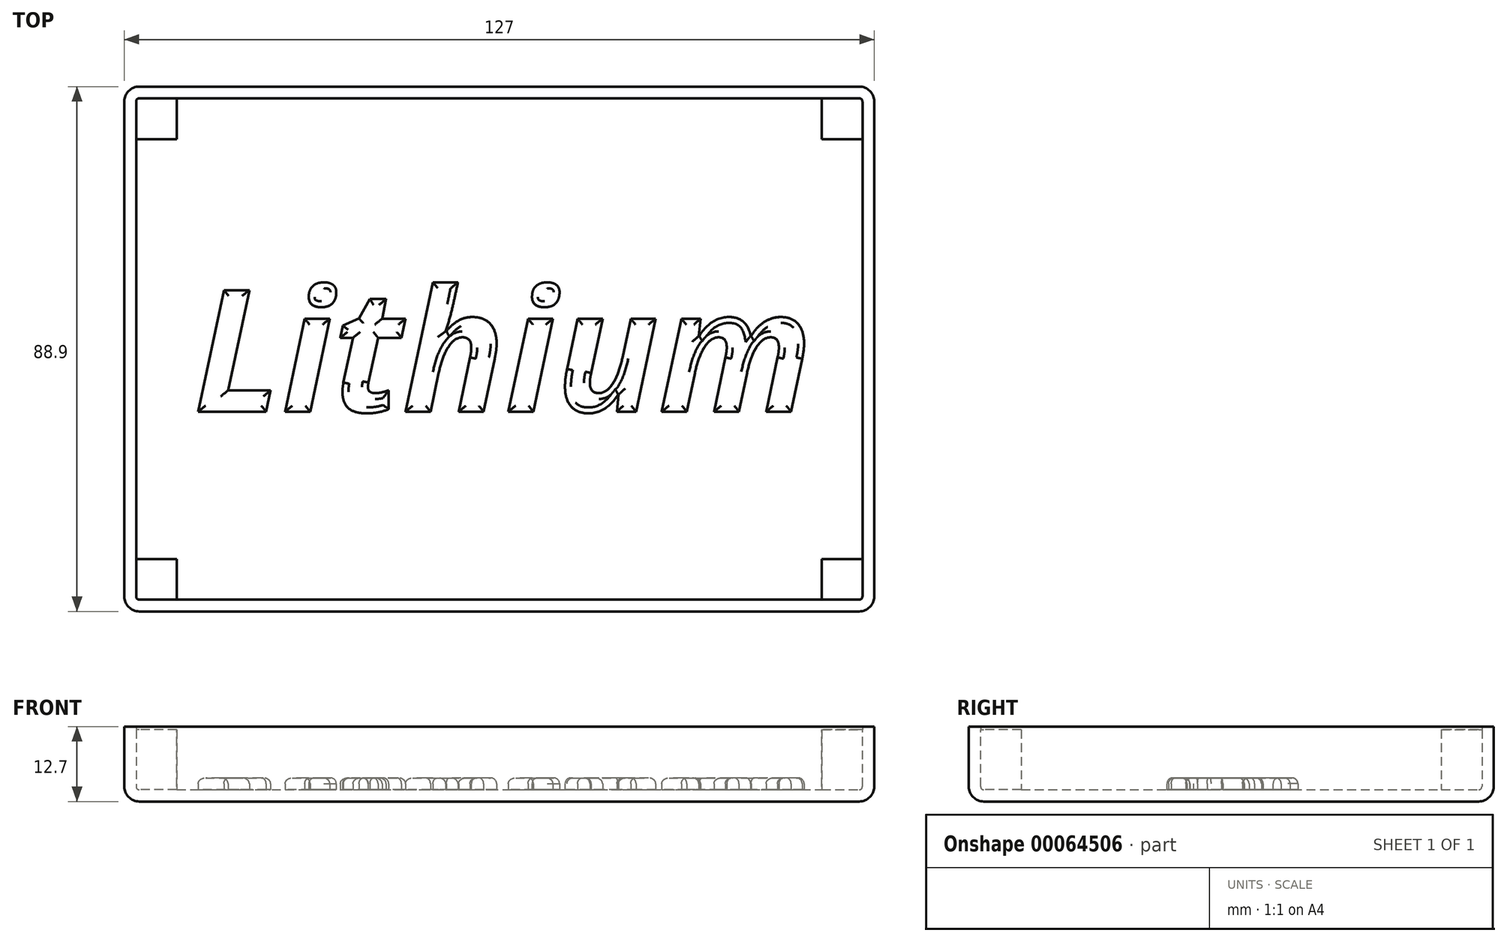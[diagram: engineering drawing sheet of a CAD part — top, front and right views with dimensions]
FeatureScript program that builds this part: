
annotation { "Feature Type Name" : "Feature", "Feature Type Description" : "" }
export const myFeature = defineFeature(function(context is Context, id is Id, definition is map)
    precondition{}
    {
        {
            var Q0;
            Q0=qCreatedBy(makeId("Top.planeOp"),FACE);
            var sketch = newSketch(context, id + "F0", { "sketchPlane" : qUnion([Q0])});
            skLineSegment(sketch, "E0.rect.bottom", {"start": v(63.5, 44.45) * mm, "end": v(-63.5, 44.45) * mm});
            skLineSegment(sketch, "E0.rect.top", {"start": v(63.5, -44.45) * mm, "end": v(-63.5, -44.45) * mm});
            skLineSegment(sketch, "E0.rect.left", {"start": v(63.5, 44.45) * mm, "end": v(63.5, -44.45) * mm});
            skLineSegment(sketch, "E0.rect.right", {"start": v(-63.5, 44.45) * mm, "end": v(-63.5, -44.45) * mm});
            skPoint(sketch, "E0.rect.middle", {"position": v(0, 0) * mm});
            skSolve(sketch);
        }
        {
            var Q0;
            Q0 = qSketchRegion(id + "F0", true);
            extrude(context, id + "F1", {"entities" : qUnion([Q0]), "depth" : 12.7 * mm});
        }
        {
            var Q0;
            Q0=makeQuery(id+"F1.opExtrude","SWEPT_EDGE",EDGE,{"disambiguationData":[OSD([sQuery(id+"F0.wireOp",EDGE,"E0.rect.top"),sQuery(id+"F0.wireOp",EDGE,"E0.rect.right")])]});
            var Q1;
            Q1=makeQuery(id+"F1.opExtrude","SWEPT_EDGE",EDGE,{"disambiguationData":[OSD([sQuery(id+"F0.wireOp",EDGE,"E0.rect.bottom"),sQuery(id+"F0.wireOp",EDGE,"E0.rect.right")])]});
            var Q2;
            Q2=makeQuery(id+"F1.opExtrude","SWEPT_EDGE",EDGE,{"disambiguationData":[OSD([sQuery(id+"F0.wireOp",EDGE,"E0.rect.bottom"),sQuery(id+"F0.wireOp",EDGE,"E0.rect.left")])]});
            var Q3;
            Q3=makeQuery(id+"F1.opExtrude","SWEPT_EDGE",EDGE,{"disambiguationData":[OSD([sQuery(id+"F0.wireOp",EDGE,"E0.rect.top"),sQuery(id+"F0.wireOp",EDGE,"E0.rect.left")])]});
            var Q4;
            Q4=makeQuery(id+"F1.opExtrude","CAP_FACE",FACE,{"disambiguationData":[OSD([sQuery(id+"F0.wireOp",EDGE,"E0.rect.bottom"),sQuery(id+"F0.wireOp",EDGE,"E0.rect.top"),sQuery(id+"F0.wireOp",EDGE,"E0.rect.left"),sQuery(id+"F0.wireOp",EDGE,"E0.rect.right")])],"isStart":true});
            fillet(context, id + "F2", {"entities" : qUnion([Q0, Q1, Q2, Q3, Q4]), "radius" : 2.54 * mm, "tangentPropagation" : true, "allowEdgeOverflow" : false});
        }
        {
            var Q0;
            Q0=makeQuery(id+"F1.opExtrude","CAP_FACE",FACE,{"disambiguationData":[OSD([sQuery(id+"F0.wireOp",EDGE,"E0.rect.bottom"),sQuery(id+"F0.wireOp",EDGE,"E0.rect.top"),sQuery(id+"F0.wireOp",EDGE,"E0.rect.left"),sQuery(id+"F0.wireOp",EDGE,"E0.rect.right")])],"isStart":false});
            shell(context, id + "F3", {"entities" : qUnion([Q0]), "thickness" : 2 * mm});
        }
        {
            var Q0;
            Q0=makeQuery(id+"F3.opShell","OFFSET_FACE",FACE,{"disambiguationData":[OSD([sQuery(id+"F0.wireOp",EDGE,"E0.rect.bottom"),sQuery(id+"F0.wireOp",EDGE,"E0.rect.top"),sQuery(id+"F0.wireOp",EDGE,"E0.rect.left"),sQuery(id+"F0.wireOp",EDGE,"E0.rect.right")])]});
            var sketch = newSketch(context, id + "F4", { "sketchPlane" : qUnion([Q0])});
            skLineSegment(sketch, "E1.bottom", {"start": v(-60.96, 41.91) * mm, "end": v(-54.61, 41.91) * mm});
            skLineSegment(sketch, "E1.top", {"start": v(-60.96, 35.56) * mm, "end": v(-54.61, 35.56) * mm});
            skLineSegment(sketch, "E1.left", {"start": v(-60.96, 41.91) * mm, "end": v(-60.96, 35.56) * mm});
            skLineSegment(sketch, "E1.right", {"start": v(-54.61, 41.91) * mm, "end": v(-54.61, 35.56) * mm});
            skLineSegment(sketch, "E2.bottom", {"start": v(-54.61, 35.56) * mm, "end": v(-62.27, 35.56) * mm});
            skLineSegment(sketch, "E2.top", {"start": v(-54.61, 43.24) * mm, "end": v(-62.27, 43.24) * mm});
            skLineSegment(sketch, "E2.left", {"start": v(-54.61, 35.56) * mm, "end": v(-54.61, 43.24) * mm});
            skLineSegment(sketch, "E2.right", {"start": v(-62.27, 35.56) * mm, "end": v(-62.27, 43.24) * mm});
            skLineSegment(sketch, "E3.MirrorCS", {"start": v(60.96, 35.56) * mm, "end": v(54.61, 35.56) * mm});
            skLineSegment(sketch, "E4.MirrorCS", {"start": v(54.61, 41.91) * mm, "end": v(54.61, 35.56) * mm});
            skLineSegment(sketch, "E5.MirrorCS", {"start": v(54.61, 35.56) * mm, "end": v(62.27, 35.56) * mm});
            skLineSegment(sketch, "E6.MirrorCS", {"start": v(62.27, 35.56) * mm, "end": v(62.27, 43.24) * mm});
            skLineSegment(sketch, "E7.MirrorCS", {"start": v(54.61, 35.56) * mm, "end": v(54.61, 43.24) * mm});
            skLineSegment(sketch, "E8.MirrorCS", {"start": v(60.96, 41.91) * mm, "end": v(54.61, 41.91) * mm});
            skLineSegment(sketch, "E9.MirrorCS", {"start": v(54.61, 43.24) * mm, "end": v(62.27, 43.24) * mm});
            skLineSegment(sketch, "E10.MirrorCS", {"start": v(60.96, 41.91) * mm, "end": v(60.96, 35.56) * mm});
            skLineSegment(sketch, "E11.MirrorCS", {"start": v(54.61, -35.56) * mm, "end": v(54.61, -43.24) * mm});
            skLineSegment(sketch, "E12.MirrorCS", {"start": v(54.61, -35.56) * mm, "end": v(62.27, -35.56) * mm});
            skLineSegment(sketch, "E13.MirrorCS", {"start": v(-60.96, -35.56) * mm, "end": v(-54.61, -35.56) * mm});
            skLineSegment(sketch, "E14.MirrorCS", {"start": v(60.96, -35.56) * mm, "end": v(54.61, -35.56) * mm});
            skLineSegment(sketch, "E15.MirrorCS", {"start": v(54.61, -41.91) * mm, "end": v(54.61, -35.56) * mm});
            skLineSegment(sketch, "E16.MirrorCS", {"start": v(60.96, -41.91) * mm, "end": v(54.61, -41.91) * mm});
            skLineSegment(sketch, "E17.MirrorCS", {"start": v(54.61, -43.24) * mm, "end": v(62.27, -43.24) * mm});
            skLineSegment(sketch, "E18.MirrorCS", {"start": v(60.96, -41.91) * mm, "end": v(60.96, -35.56) * mm});
            skLineSegment(sketch, "E19.MirrorCS", {"start": v(-54.61, -41.91) * mm, "end": v(-54.61, -35.56) * mm});
            skLineSegment(sketch, "E20.MirrorCS", {"start": v(-54.61, -35.56) * mm, "end": v(-62.27, -35.56) * mm});
            skLineSegment(sketch, "E21.MirrorCS", {"start": v(62.27, -35.56) * mm, "end": v(62.27, -43.24) * mm});
            skLineSegment(sketch, "E22.MirrorCS", {"start": v(-60.96, -41.91) * mm, "end": v(-54.61, -41.91) * mm});
            skLineSegment(sketch, "E23.MirrorCS", {"start": v(-60.96, -41.91) * mm, "end": v(-60.96, -35.56) * mm});
            skLineSegment(sketch, "E24.MirrorCS", {"start": v(-54.61, -43.24) * mm, "end": v(-62.27, -43.24) * mm});
            skLineSegment(sketch, "E25.MirrorCS", {"start": v(-54.61, -35.56) * mm, "end": v(-54.61, -43.24) * mm});
            skLineSegment(sketch, "E26.MirrorCS", {"start": v(-62.27, -35.56) * mm, "end": v(-62.27, -43.24) * mm});
            skSolve(sketch);
        }
        {
            var Q0;
            Q0 = qSketchRegion(id + "F4", true);
            extrude(context, id + "F5", {"entities" : qUnion([Q0]), "operationType" : NewBodyOperationType.ADD, "depth" : 10.16 * mm});
        }
        {
            var Q0;
            Q0=makeQuery(id+"F3.opShell","OFFSET_FACE",FACE,{"disambiguationData":[OSD([sQuery(id+"F0.wireOp",EDGE,"E0.rect.bottom"),sQuery(id+"F0.wireOp",EDGE,"E0.rect.top"),sQuery(id+"F0.wireOp",EDGE,"E0.rect.left"),sQuery(id+"F0.wireOp",EDGE,"E0.rect.right")])]});
            var sketch = newSketch(context, id + "F6", { "sketchPlane" : qUnion([Q0])});
            skText(sketch, "E27", { "text": "Lithium", "fontName": "OpenSans-BoldItalic.ttf"});
            const initialGuessF6  = {"E27": [-0.05173, -0.01062, 1, 0, 0.02076]};
            skSetInitialGuess(sketch, initialGuessF6);
            skSolve(sketch);
        }
        {
            var Q0;
            Q0 = qSketchRegion(id + "F6", true);
            extrude(context, id + "F7", {"entities" : qUnion([Q0]), "operationType" : NewBodyOperationType.ADD, "depth" : 2 * mm});
        }
        {
            var Q0;
            Q0=makeQuery(id+"F7.opExtrude","CAP_FACE",FACE,{"disambiguationData":[OSD([sQuery(id+"F6.wireOp",EDGE,"E27.sketch_text.stroke-0"),sQuery(id+"F6.wireOp",EDGE,"E27.sketch_text.stroke-1"),sQuery(id+"F6.wireOp",EDGE,"E27.sketch_text.stroke-2"),sQuery(id+"F6.wireOp",EDGE,"E27.sketch_text.stroke-3"),sQuery(id+"F6.wireOp",EDGE,"E27.sketch_text.stroke-4"),sQuery(id+"F6.wireOp",EDGE,"E27.sketch_text.stroke-5")])],"isStart":false});
            var Q1;
            Q1=makeQuery(id+"F7.opExtrude","CAP_FACE",FACE,{"disambiguationData":[OSD([sQuery(id+"F6.wireOp",EDGE,"E27.sketch_text.stroke-13"),sQuery(id+"F6.wireOp",EDGE,"E27.sketch_text.stroke-14"),sQuery(id+"F6.wireOp",EDGE,"E27.sketch_text.stroke-15"),sQuery(id+"F6.wireOp",EDGE,"E27.sketch_text.stroke-16")])],"isStart":false});
            var Q2;
            Q2=makeQuery(id+"F7.opExtrude","CAP_FACE",FACE,{"disambiguationData":[OSD([sQuery(id+"F6.wireOp",EDGE,"E27.sketch_text.stroke-6"),sQuery(id+"F6.wireOp",EDGE,"E27.sketch_text.stroke-7"),sQuery(id+"F6.wireOp",EDGE,"E27.sketch_text.stroke-8"),sQuery(id+"F6.wireOp",EDGE,"E27.sketch_text.stroke-9"),sQuery(id+"F6.wireOp",EDGE,"E27.sketch_text.stroke-10"),sQuery(id+"F6.wireOp",EDGE,"E27.sketch_text.stroke-11"),sQuery(id+"F6.wireOp",EDGE,"E27.sketch_text.stroke-12")])],"isStart":false});
            var Q3;
            Q3=makeQuery(id+"F7.opExtrude","CAP_FACE",FACE,{"disambiguationData":[OSD([sQuery(id+"F6.wireOp",EDGE,"E27.sketch_text.stroke-17"),sQuery(id+"F6.wireOp",EDGE,"E27.sketch_text.stroke-18"),sQuery(id+"F6.wireOp",EDGE,"E27.sketch_text.stroke-19"),sQuery(id+"F6.wireOp",EDGE,"E27.sketch_text.stroke-20"),sQuery(id+"F6.wireOp",EDGE,"E27.sketch_text.stroke-21"),sQuery(id+"F6.wireOp",EDGE,"E27.sketch_text.stroke-22"),sQuery(id+"F6.wireOp",EDGE,"E27.sketch_text.stroke-23"),sQuery(id+"F6.wireOp",EDGE,"E27.sketch_text.stroke-24"),sQuery(id+"F6.wireOp",EDGE,"E27.sketch_text.stroke-25"),sQuery(id+"F6.wireOp",EDGE,"E27.sketch_text.stroke-26"),sQuery(id+"F6.wireOp",EDGE,"E27.sketch_text.stroke-27"),sQuery(id+"F6.wireOp",EDGE,"E27.sketch_text.stroke-28"),sQuery(id+"F6.wireOp",EDGE,"E27.sketch_text.stroke-29"),sQuery(id+"F6.wireOp",EDGE,"E27.sketch_text.stroke-30"),sQuery(id+"F6.wireOp",EDGE,"E27.sketch_text.stroke-31"),sQuery(id+"F6.wireOp",EDGE,"E27.sketch_text.stroke-32"),sQuery(id+"F6.wireOp",EDGE,"E27.sketch_text.stroke-33"),sQuery(id+"F6.wireOp",EDGE,"E27.sketch_text.stroke-34"),sQuery(id+"F6.wireOp",EDGE,"E27.sketch_text.stroke-35")])],"isStart":false});
            var Q4;
            Q4=makeQuery(id+"F7.opExtrude","CAP_FACE",FACE,{"disambiguationData":[OSD([sQuery(id+"F6.wireOp",EDGE,"E27.sketch_text.stroke-36"),sQuery(id+"F6.wireOp",EDGE,"E27.sketch_text.stroke-37"),sQuery(id+"F6.wireOp",EDGE,"E27.sketch_text.stroke-38"),sQuery(id+"F6.wireOp",EDGE,"E27.sketch_text.stroke-39"),sQuery(id+"F6.wireOp",EDGE,"E27.sketch_text.stroke-40"),sQuery(id+"F6.wireOp",EDGE,"E27.sketch_text.stroke-41"),sQuery(id+"F6.wireOp",EDGE,"E27.sketch_text.stroke-42"),sQuery(id+"F6.wireOp",EDGE,"E27.sketch_text.stroke-43"),sQuery(id+"F6.wireOp",EDGE,"E27.sketch_text.stroke-44"),sQuery(id+"F6.wireOp",EDGE,"E27.sketch_text.stroke-45"),sQuery(id+"F6.wireOp",EDGE,"E27.sketch_text.stroke-46"),sQuery(id+"F6.wireOp",EDGE,"E27.sketch_text.stroke-47"),sQuery(id+"F6.wireOp",EDGE,"E27.sketch_text.stroke-48"),sQuery(id+"F6.wireOp",EDGE,"E27.sketch_text.stroke-49"),sQuery(id+"F6.wireOp",EDGE,"E27.sketch_text.stroke-50"),sQuery(id+"F6.wireOp",EDGE,"E27.sketch_text.stroke-51"),sQuery(id+"F6.wireOp",EDGE,"E27.sketch_text.stroke-52"),sQuery(id+"F6.wireOp",EDGE,"E27.sketch_text.stroke-53"),sQuery(id+"F6.wireOp",EDGE,"E27.sketch_text.stroke-54")])],"isStart":false});
            var Q5;
            Q5=makeQuery(id+"F7.opExtrude","CAP_FACE",FACE,{"disambiguationData":[OSD([sQuery(id+"F6.wireOp",EDGE,"E27.sketch_text.stroke-62"),sQuery(id+"F6.wireOp",EDGE,"E27.sketch_text.stroke-63"),sQuery(id+"F6.wireOp",EDGE,"E27.sketch_text.stroke-64"),sQuery(id+"F6.wireOp",EDGE,"E27.sketch_text.stroke-65")])],"isStart":false});
            var Q6;
            Q6=makeQuery(id+"F7.opExtrude","CAP_FACE",FACE,{"disambiguationData":[OSD([sQuery(id+"F6.wireOp",EDGE,"E27.sketch_text.stroke-55"),sQuery(id+"F6.wireOp",EDGE,"E27.sketch_text.stroke-56"),sQuery(id+"F6.wireOp",EDGE,"E27.sketch_text.stroke-57"),sQuery(id+"F6.wireOp",EDGE,"E27.sketch_text.stroke-58"),sQuery(id+"F6.wireOp",EDGE,"E27.sketch_text.stroke-59"),sQuery(id+"F6.wireOp",EDGE,"E27.sketch_text.stroke-60"),sQuery(id+"F6.wireOp",EDGE,"E27.sketch_text.stroke-61")])],"isStart":false});
            var Q7;
            Q7=makeQuery(id+"F7.opExtrude","CAP_FACE",FACE,{"disambiguationData":[OSD([sQuery(id+"F6.wireOp",EDGE,"E27.sketch_text.stroke-66"),sQuery(id+"F6.wireOp",EDGE,"E27.sketch_text.stroke-67"),sQuery(id+"F6.wireOp",EDGE,"E27.sketch_text.stroke-68"),sQuery(id+"F6.wireOp",EDGE,"E27.sketch_text.stroke-69"),sQuery(id+"F6.wireOp",EDGE,"E27.sketch_text.stroke-70"),sQuery(id+"F6.wireOp",EDGE,"E27.sketch_text.stroke-71"),sQuery(id+"F6.wireOp",EDGE,"E27.sketch_text.stroke-72"),sQuery(id+"F6.wireOp",EDGE,"E27.sketch_text.stroke-73"),sQuery(id+"F6.wireOp",EDGE,"E27.sketch_text.stroke-74"),sQuery(id+"F6.wireOp",EDGE,"E27.sketch_text.stroke-75"),sQuery(id+"F6.wireOp",EDGE,"E27.sketch_text.stroke-76"),sQuery(id+"F6.wireOp",EDGE,"E27.sketch_text.stroke-77"),sQuery(id+"F6.wireOp",EDGE,"E27.sketch_text.stroke-78"),sQuery(id+"F6.wireOp",EDGE,"E27.sketch_text.stroke-79"),sQuery(id+"F6.wireOp",EDGE,"E27.sketch_text.stroke-80"),sQuery(id+"F6.wireOp",EDGE,"E27.sketch_text.stroke-81"),sQuery(id+"F6.wireOp",EDGE,"E27.sketch_text.stroke-82")])],"isStart":false});
            var Q8;
            Q8=makeQuery(id+"F7.opExtrude","CAP_FACE",FACE,{"disambiguationData":[OSD([sQuery(id+"F6.wireOp",EDGE,"E27.sketch_text.stroke-83"),sQuery(id+"F6.wireOp",EDGE,"E27.sketch_text.stroke-84"),sQuery(id+"F6.wireOp",EDGE,"E27.sketch_text.stroke-85"),sQuery(id+"F6.wireOp",EDGE,"E27.sketch_text.stroke-86"),sQuery(id+"F6.wireOp",EDGE,"E27.sketch_text.stroke-87"),sQuery(id+"F6.wireOp",EDGE,"E27.sketch_text.stroke-88"),sQuery(id+"F6.wireOp",EDGE,"E27.sketch_text.stroke-89"),sQuery(id+"F6.wireOp",EDGE,"E27.sketch_text.stroke-90"),sQuery(id+"F6.wireOp",EDGE,"E27.sketch_text.stroke-91"),sQuery(id+"F6.wireOp",EDGE,"E27.sketch_text.stroke-92"),sQuery(id+"F6.wireOp",EDGE,"E27.sketch_text.stroke-93"),sQuery(id+"F6.wireOp",EDGE,"E27.sketch_text.stroke-94"),sQuery(id+"F6.wireOp",EDGE,"E27.sketch_text.stroke-95"),sQuery(id+"F6.wireOp",EDGE,"E27.sketch_text.stroke-96"),sQuery(id+"F6.wireOp",EDGE,"E27.sketch_text.stroke-97"),sQuery(id+"F6.wireOp",EDGE,"E27.sketch_text.stroke-98"),sQuery(id+"F6.wireOp",EDGE,"E27.sketch_text.stroke-99"),sQuery(id+"F6.wireOp",EDGE,"E27.sketch_text.stroke-100"),sQuery(id+"F6.wireOp",EDGE,"E27.sketch_text.stroke-101"),sQuery(id+"F6.wireOp",EDGE,"E27.sketch_text.stroke-102"),sQuery(id+"F6.wireOp",EDGE,"E27.sketch_text.stroke-103"),sQuery(id+"F6.wireOp",EDGE,"E27.sketch_text.stroke-104"),sQuery(id+"F6.wireOp",EDGE,"E27.sketch_text.stroke-105"),sQuery(id+"F6.wireOp",EDGE,"E27.sketch_text.stroke-106"),sQuery(id+"F6.wireOp",EDGE,"E27.sketch_text.stroke-107"),sQuery(id+"F6.wireOp",EDGE,"E27.sketch_text.stroke-108"),sQuery(id+"F6.wireOp",EDGE,"E27.sketch_text.stroke-109"),sQuery(id+"F6.wireOp",EDGE,"E27.sketch_text.stroke-110")])],"isStart":false});
            fillet(context, id + "F8", {"entities" : qUnion([Q0, Q1, Q2, Q3, Q4, Q5, Q6, Q7, Q8]), "radius" : 1 * mm, "tangentPropagation" : true, "allowEdgeOverflow" : false});
        }
    });
